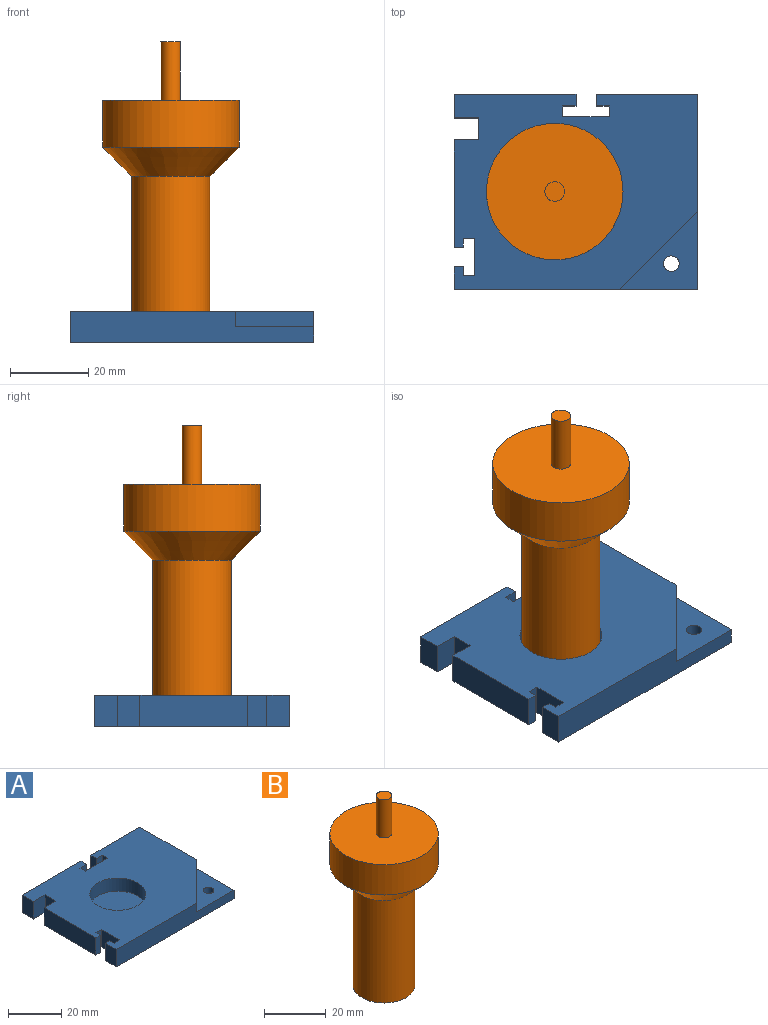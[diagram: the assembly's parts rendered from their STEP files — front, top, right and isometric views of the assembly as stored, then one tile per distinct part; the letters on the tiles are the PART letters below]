
ASSEMBLY  parts=2 mates=1
PART A: 31 faces, bbox 62.5x50x8 mm
  f0: plane 20x20mm, normal (0.71,-0.71,0), area 113.1mm2, adj f1,f25,f26,f29
  f1: plane 50x8mm, normal (1,0,0), area 320mm2, adj f0,f2,f25,f26,f27,f29
  f2: plane 25.98x8mm, normal (0,1,0), area 207.8mm2, adj f1,f3,f26,f27
  f3: plane 8x2.97mm, normal (-1,0,0), area 23.8mm2, adj f2,f4,f26,f27
  f4: plane 8x3.26mm, normal (0,-1,0), area 26.1mm2, adj f3,f5,f26,f27
  f5: plane 8x2.75mm, normal (-1,0,0), area 22mm2, adj f4,f6,f26,f27
  f6: plane 11.98x8mm, normal (0,1,0), area 95.8mm2, adj f5,f7,f26,f27
  f7: plane 8x2.75mm, normal (1,0,0), area 22mm2, adj f6,f8,f26,f27
  f8: plane 8x3.45mm, normal (0,-1,0), area 27.6mm2, adj f7,f9,f26,f27
  f9: plane 8x2.97mm, normal (1,0,0), area 23.8mm2, adj f8,f10,f26,f27
  f10: plane 31.25x8mm, normal (0,1,0), area 250mm2, adj f9,f11,f26,f27
  f11: plane 8x6.04mm, normal (-1,0,0), area 48.3mm2, adj f10,f12,f26,f27
  f12: plane 8x6.19mm, normal (0,-1,0), area 49.5mm2, adj f11,f13,f26,f27
  f13: plane 8x5.64mm, normal (-1,0,0), area 45.1mm2, adj f12,f14,f26,f27
  f14: plane 8x6.19mm, normal (0,1,0), area 49.5mm2, adj f13,f15,f26,f27
  f15: plane 27.49x8mm, normal (-1,0,0), area 219.9mm2, adj f14,f16,f26,f27
  f16: plane 8x2.38mm, normal (0,-1,0), area 19mm2, adj f15,f17,f26,f27
  f17: plane 8x2.3mm, normal (1,0,0), area 18.4mm2, adj f16,f18,f26,f27
  f18: plane 8x2.86mm, normal (0,-1,0), area 22.9mm2, adj f17,f19,f26,f27
  f19: plane 9.63x8mm, normal (-1,0,0), area 77mm2, adj f18,f20,f26,f27
  f20: plane 8x2.86mm, normal (0,1,0), area 22.9mm2, adj f19,f21,f26,f27
  f21: plane 8x2.33mm, normal (1,0,0), area 18.6mm2, adj f20,f22,f26,f27
  f22: plane 8x2.38mm, normal (0,1,0), area 19mm2, adj f21,f23,f26,f27
  f23: plane 8x5.84mm, normal (-1,0,0), area 46.7mm2, adj f22,f25,f26,f27
  f24: cylinder r=10.5mm len=21mm, axis (0,0,-1), area 395.8mm2, adj f26,f30
  f25: plane 62.5x8mm, normal (0,-1,0), area 420mm2, adj f0,f1,f23,f26,f27,f29
  f26: plane 62.5x50mm, normal (0,0,1), area 2455.7mm2, adj f0,f1,f2,f3,f4,f5,f6,f7
  f27: plane 62.5x50mm, normal (0,0,-1), area 2989.5mm2, adj f1,f2,f3,f4,f5,f6,f7,f8
  f28: cylinder r=2mm len=4mm, axis (0,0,-1), area 50.3mm2, adj f27,f29
  f29: plane 20x20mm, normal (0,0,1), area 187.4mm2, adj f0,f1,f25,f28
  f30: plane 21x21mm, normal (0,0,1), area 346.4mm2, adj f24
PART B: 7 faces, bbox 35x35x75 mm
  f0: cylinder r=17.5mm len=35mm, axis (0,0,-1), area 1319.5mm2, adj f1,f5
  f1: plane 35x35mm, normal (0,0,1), area 942.5mm2, adj f0,f3
  f2: cylinder r=10mm len=40.5mm, axis (0,0,-1), area 2544.7mm2, adj f5,f6
  f3: cylinder r=2.5mm len=15mm, axis (0,0,-1), area 235.6mm2, adj f1,f4
  f4: plane 5x5mm, normal (0,0,1), area 19.6mm2, adj f3
  f5: cone r=17.5mm half-angle=45deg, axis (0,0,1), area 916.3mm2, adj f0,f2
  f6: plane 20x20mm, normal (0,0,-1), area 314.2mm2, adj f2
PLACE A t=(-6.74,6.51,27.74)mm
PLACE B t=(36.56,-18.49,49.74)mm
MATE fastened B.f2 <-> A.f24  axis (0,0,-1) through (36.56,-18.49,29.74)mm
